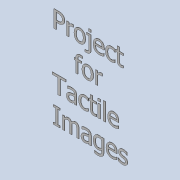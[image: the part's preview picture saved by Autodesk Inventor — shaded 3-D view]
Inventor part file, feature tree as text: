
AUTODESK INVENTOR PART (.ipt)
format: ipt  version: 2020 (Build 240168000, 168)  size: 665,088 bytes
history: native  units: mm
features: extrude x1, sketch x1
ambient origin geometry x8: Origin, YZ Plane, XZ Plane, XY Plane, X Axis, Y Axis, Z Axis, Center Point
bodies: Solid1 (feature_tree)
feature tree (2):
  extrude  "Extrusion1"  Depth=200.0mm
  sketch  "Sketch1"  dims[d0=300.0mm d1=200.0mm d2=0.6mm d3=0.0mm d4=50.0mm d5=50.0mm d6=20.0mm]
